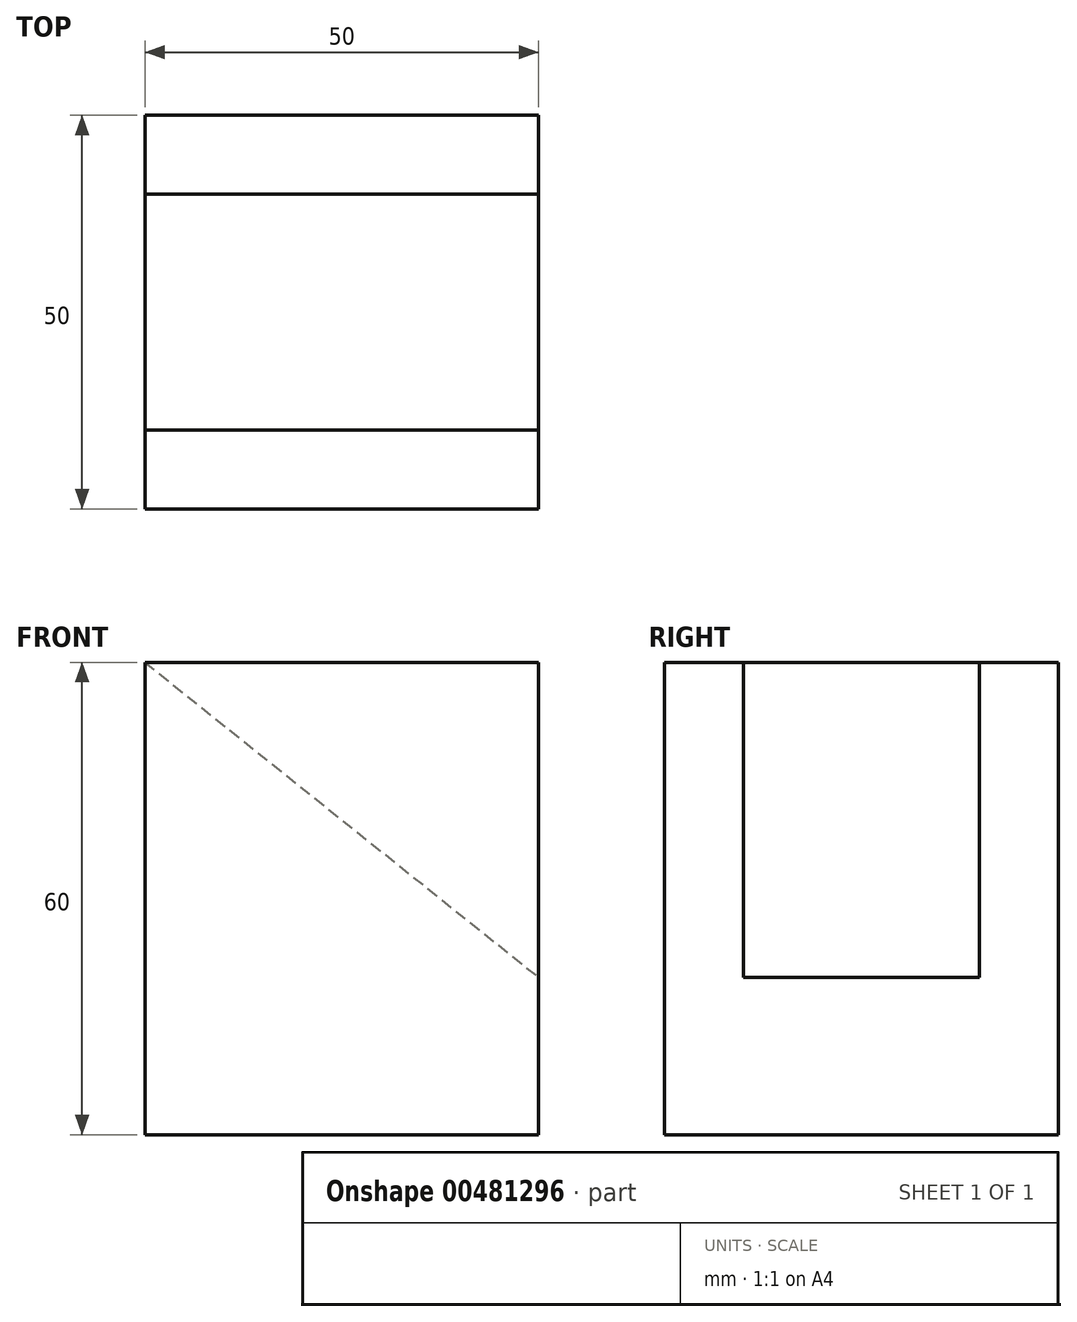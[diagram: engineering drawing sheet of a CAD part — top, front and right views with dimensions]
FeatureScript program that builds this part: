
annotation { "Feature Type Name" : "Feature", "Feature Type Description" : "" }
export const myFeature = defineFeature(function(context is Context, id is Id, definition is map)
    precondition{}
    {
        {
            var Q0;
            Q0=qCreatedBy(makeId("Right.planeOp"),FACE);
            var sketch = newSketch(context, id + "F0", { "sketchPlane" : qUnion([Q0])});
            skLineSegment(sketch, "E0", {"start": v(0, 0) * mm, "end": v(0, 60) * mm});
            skLineSegment(sketch, "E1", {"start": v(0, 60) * mm, "end": v(10, 60) * mm});
            skLineSegment(sketch, "E2", {"start": v(10, 60) * mm, "end": v(10, 20) * mm});
            skLineSegment(sketch, "E3", {"start": v(10, 20) * mm, "end": v(40, 20) * mm});
            skLineSegment(sketch, "E4", {"start": v(40, 20) * mm, "end": v(40, 60) * mm});
            skLineSegment(sketch, "E5", {"start": v(40, 60) * mm, "end": v(50, 60) * mm});
            skLineSegment(sketch, "E6", {"start": v(50, 60) * mm, "end": v(50, 0) * mm});
            skLineSegment(sketch, "E7", {"start": v(50, 0) * mm, "end": v(0, 0) * mm});
            skSolve(sketch);
        }
        {
            var Q0;
            Q0=makeQuery(id+"F0.imprint","IMPRINT",FACE,{"disambiguationData":[TD([[makeQuery(id+"F0.imprint","IMPRINT",EDGE,{"derivedFrom":sQuery(id+"F0.wireOp",EDGE,"E0")}),-1.0]])]});
            extrude(context, id + "F1", {"entities" : qUnion([Q0]), "depth" : 50 * mm});
        }
        {
            var Q0;
            Q0=makeQuery(id+"F1.opExtrude","SWEPT_FACE",FACE,{"disambiguationData":[OSD([sQuery(id+"F0.wireOp",EDGE,"E0")])]});
            var sketch = newSketch(context, id + "F2", { "sketchPlane" : qUnion([Q0])});
            skLineSegment(sketch, "E8", {"start": v(0, 60) * mm, "end": v(50, 20) * mm});
            skLineSegment(sketch, "E9", {"start": v(50, 20) * mm, "end": v(0, 20) * mm});
            skLineSegment(sketch, "E10", {"start": v(0, 20) * mm, "end": v(0, 60) * mm});
            skSolve(sketch);
        }
        {
            var Q0;
            Q0=makeQuery(id+"F2.imprint","IMPRINT",FACE,{"disambiguationData":[TD([[makeQuery(id+"F2.imprint","IMPRINT",EDGE,{"derivedFrom":sQuery(id+"F2.wireOp",EDGE,"E8")}),-1.0]])]});
            extrude(context, id + "F3", {"entities" : qUnion([Q0]), "operationType" : NewBodyOperationType.ADD, "oppositeDirection" : true, "depth" : 40 * mm});
        }
    });
